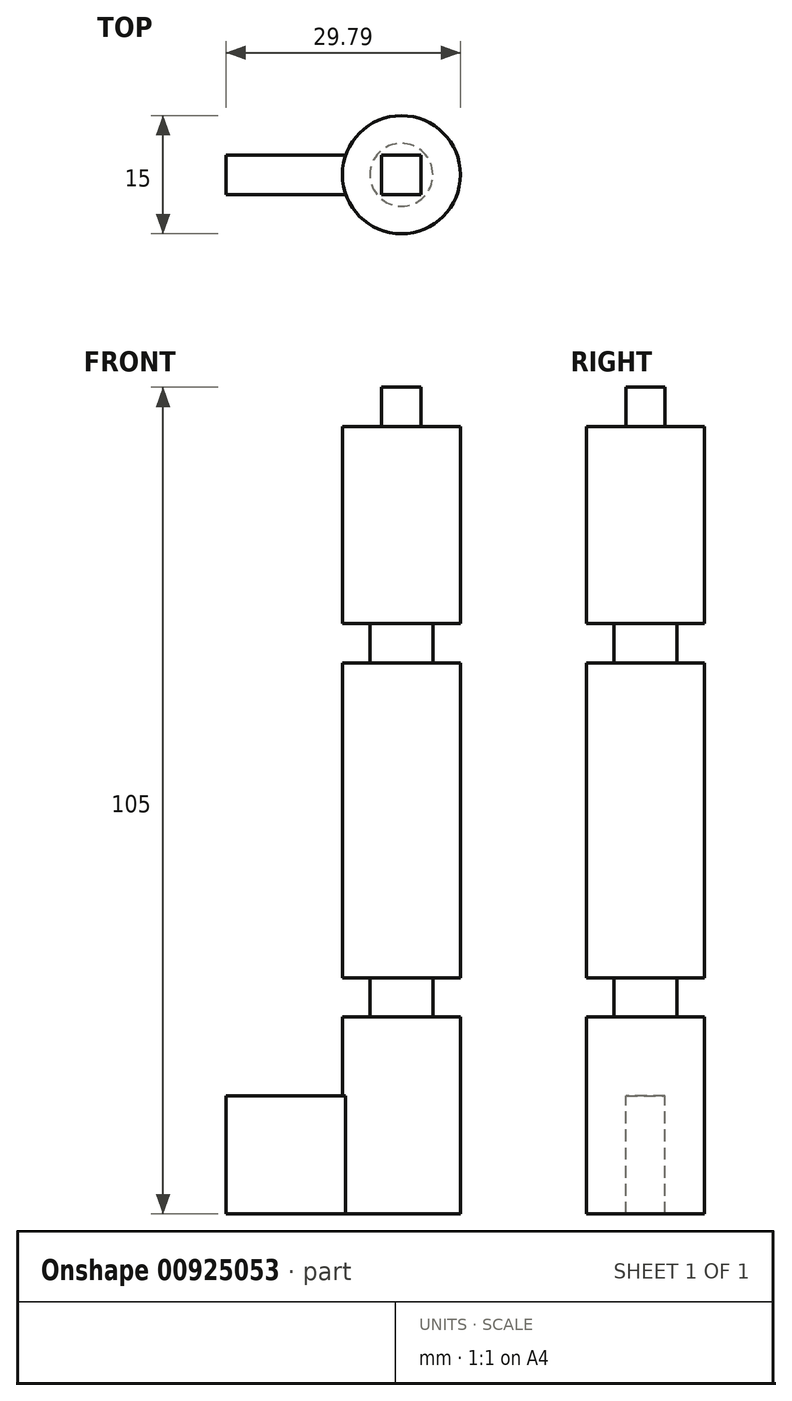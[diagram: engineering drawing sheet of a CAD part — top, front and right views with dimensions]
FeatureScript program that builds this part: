
annotation { "Feature Type Name" : "Feature", "Feature Type Description" : "" }
export const myFeature = defineFeature(function(context is Context, id is Id, definition is map)
    precondition{}
    {
        {
            var Q0;
            Q0=qCreatedBy(makeId("Top.planeOp"),FACE);
            var sketch = newSketch(context, id + "F0", { "sketchPlane" : qUnion([Q0])});
            skCircle(sketch, "E0", {"center": v(0, 0) * mm, "radius": 7.5 * mm});
            skSolve(sketch);
        }
        {
            var Q0;
            Q0 = qSketchRegion(id + "F0", true);
            extrude(context, id + "F1", {"entities" : qUnion([Q0]), "depth" : 20 * mm, "offsetDistance" : 25 * mm});
        }
        {
            var Q0;
            Q0=makeQuery(id+"F1.opExtrude","CAP_FACE",FACE,{"disambiguationData":[OSD([sQuery(id+"F0.wireOp",EDGE,"E0")])],"isStart":false});
            var sketch = newSketch(context, id + "F2", { "sketchPlane" : qUnion([Q0])});
            skCircle(sketch, "E1", {"center": v(0, 0) * mm, "radius": 4 * mm});
            skSolve(sketch);
        }
        {
            var Q0;
            Q0 = qSketchRegion(id + "F2", true);
            extrude(context, id + "F3", {"entities" : qUnion([Q0]), "operationType" : NewBodyOperationType.ADD, "depth" : 5 * mm, "offsetDistance" : 25 * mm});
        }
        {
            var Q0;
            Q0=makeQuery(id+"F3.opExtrude","CAP_FACE",FACE,{"disambiguationData":[OSD([sQuery(id+"F2.wireOp",EDGE,"E1")])],"isStart":false});
            var sketch = newSketch(context, id + "F4", { "sketchPlane" : qUnion([Q0])});
            skCircle(sketch, "E2", {"center": v(0, 0) * mm, "radius": 7.5 * mm});
            skSolve(sketch);
        }
        {
            var Q0;
            Q0=makeQuery(id+"F4.imprint","IMPRINT",FACE,{"disambiguationData":[TD([[makeQuery(id+"F4.imprint","IMPRINT",EDGE,{"derivedFrom":sQuery(id+"F4.wireOp",EDGE,"E2")}),1.0]])]});
            var Q1;
            Q1=makeQuery(id+"F4.imprint","IMPRINT",FACE,{"disambiguationData":[TD([[makeQuery(id+"F4.imprint","IMPRINT",EDGE,{"derivedFrom":makeQuery(id+"F3.opExtrude","CAP_EDGE",EDGE,{"disambiguationData":[OSD([sQuery(id+"F2.wireOp",EDGE,"E1")])],"isStart":false})}),1.0]])]});
            extrude(context, id + "F5", {"entities" : qUnion([Q0, Q1]), "operationType" : NewBodyOperationType.ADD, "depth" : 25 * mm, "offsetDistance" : 25 * mm});
        }
        {
            var Q0;
            Q0=makeQuery(id+"F1.opExtrude","SWEPT_BODY",BODY,{"disambiguationData":[OSD([sQuery(id+"F0.wireOp",EDGE,"E0")])]});
            var Q1;
            Q1=qCreatedBy(makeId("Top.planeOp"),FACE);
            mirror(context, id + "F6", {"operationType" : NewBodyOperationType.ADD, "entities" : qUnion([Q0]), "mirrorPlane" : qUnion([Q1])});
        }
        {
            var Q0;
            Q0=makeQuery(id+"F5.opExtrude","CAP_FACE",FACE,{"disambiguationData":[OSD([sQuery(id+"F4.wireOp",EDGE,"E2")])],"isStart":false});
            var sketch = newSketch(context, id + "F7", { "sketchPlane" : qUnion([Q0])});
            skLineSegment(sketch, "E3.bottom", {"start": v(-2.5, -2.5) * mm, "end": v(2.5, -2.5) * mm});
            skLineSegment(sketch, "E3.top", {"start": v(-2.5, 2.5) * mm, "end": v(2.5, 2.5) * mm});
            skLineSegment(sketch, "E3.left", {"start": v(-2.5, -2.5) * mm, "end": v(-2.5, 2.5) * mm});
            skLineSegment(sketch, "E3.right", {"start": v(2.5, -2.5) * mm, "end": v(2.5, 2.5) * mm});
            skSolve(sketch);
        }
        {
            var Q0;
            Q0=makeQuery(id+"F7.imprint","IMPRINT",FACE,{"disambiguationData":[TD([[makeQuery(id+"F7.imprint","IMPRINT",EDGE,{"derivedFrom":sQuery(id+"F7.wireOp",EDGE,"E3.bottom")}),1.0]])]});
            extrude(context, id + "F8", {"entities" : qUnion([Q0]), "operationType" : NewBodyOperationType.ADD, "depth" : 5 * mm, "offsetDistance" : 25 * mm});
        }
        {
            var Q0;
            Q0=makeQuery(id+"F6.opPattern","COPY",FACE,{"derivedFrom":makeQuery(id+"F5.opExtrude","CAP_FACE",FACE,{"disambiguationData":[OSD([sQuery(id+"F4.wireOp",EDGE,"E2")])],"isStart":false}),"instanceName":"1"});
            var sketch = newSketch(context, id + "F9", { "sketchPlane" : qUnion([Q0])});
            skLineSegment(sketch, "E4.bottom", {"start": v(2.5, -2.5) * mm, "end": v(-22.3, -2.5) * mm});
            skLineSegment(sketch, "E4.top", {"start": v(2.5, 2.5) * mm, "end": v(-22.3, 2.5) * mm});
            skLineSegment(sketch, "E4.left", {"start": v(2.5, -2.5) * mm, "end": v(2.5, 2.5) * mm});
            skLineSegment(sketch, "E4.right", {"start": v(-22.3, -2.5) * mm, "end": v(-22.3, 2.5) * mm});
            skSolve(sketch);
        }
        {
            var Q0;
            Q0 = qSketchRegion(id + "F9", true);
            extrude(context, id + "F10", {"entities" : qUnion([Q0]), "operationType" : NewBodyOperationType.ADD, "oppositeDirection" : true, "depth" : 15 * mm, "offsetDistance" : 25 * mm});
        }
    });
